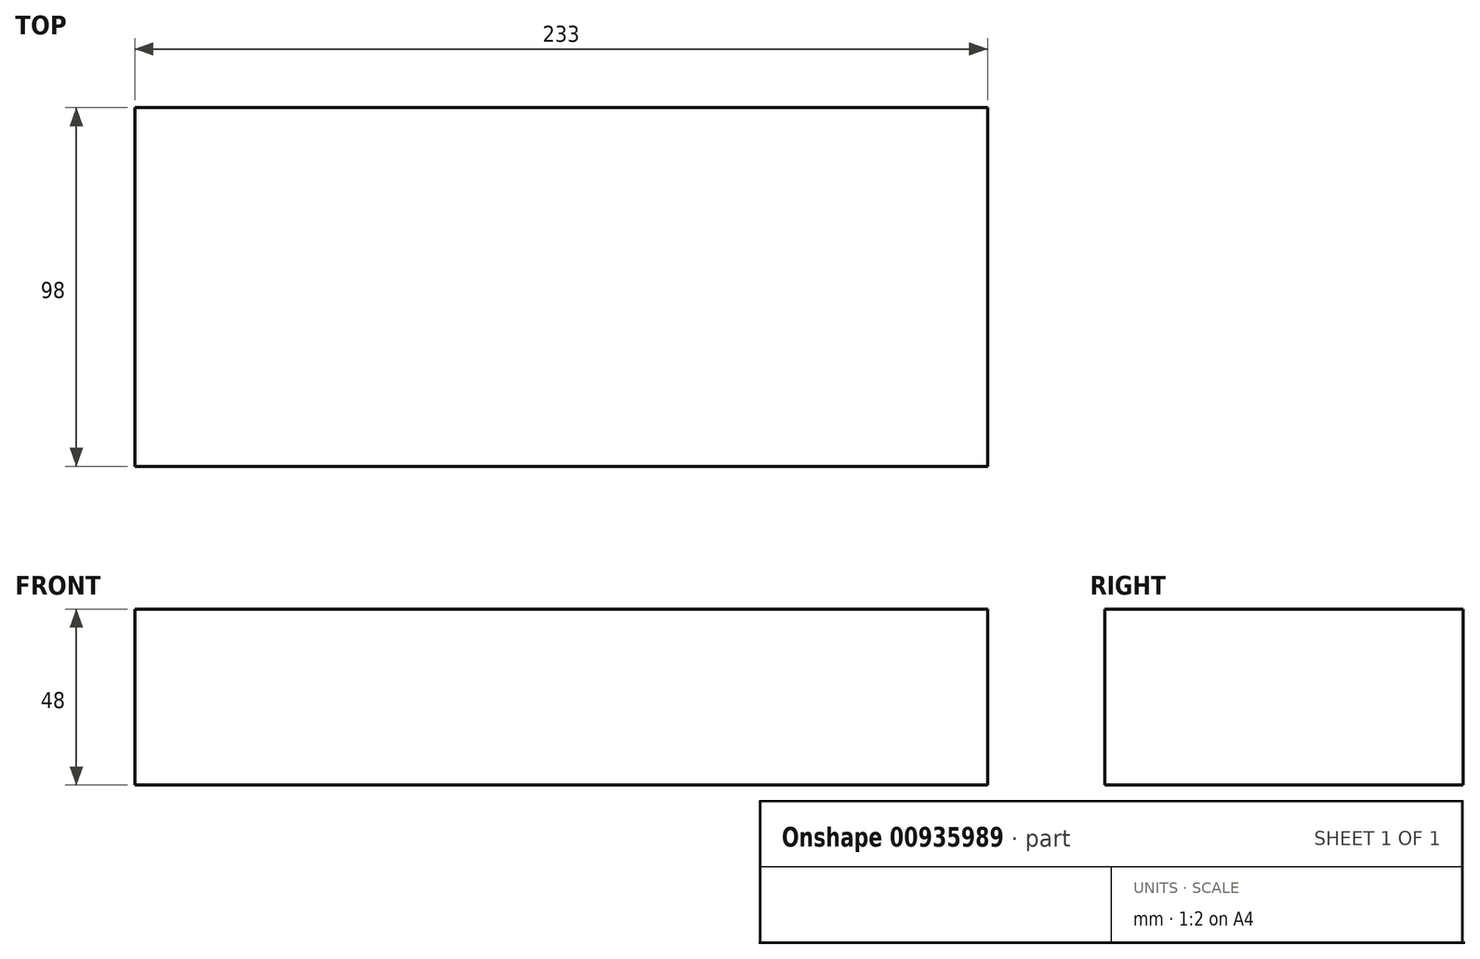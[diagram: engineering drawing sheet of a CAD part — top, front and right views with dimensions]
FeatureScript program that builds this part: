
annotation { "Feature Type Name" : "Feature", "Feature Type Description" : "" }
export const myFeature = defineFeature(function(context is Context, id is Id, definition is map)
    precondition{}
    {
        {
            var Q0;
            Q0=qCreatedBy(makeId("Right.planeOp"),FACE);
            var sketch = newSketch(context, id + "F0", { "sketchPlane" : qUnion([Q0])});
            skLineSegment(sketch, "E0.bottom", {"start": v(49, -24) * mm, "end": v(-49, -24) * mm});
            skLineSegment(sketch, "E0.top", {"start": v(49, 24) * mm, "end": v(-49, 24) * mm});
            skLineSegment(sketch, "E0.left", {"start": v(49, -24) * mm, "end": v(49, 24) * mm});
            skLineSegment(sketch, "E0.right", {"start": v(-49, -24) * mm, "end": v(-49, 24) * mm});
            skPoint(sketch, "E0.middle", {"position": v(0, 0) * mm});
            skSolve(sketch);
        }
        {
            assignVariable(context, id + "F1", {"name" : "Length", "anyValue" : 233});
        }
        {
            var Q0;
            Q0=qSketchRegion(id+"F0",true);
            extrude(context, id + "F2", {"entities" : qUnion([Q0]), "depth" : (getVariable(context, 'Length')) * mm, "offsetDistance" : 25 * mm});
        }
    });
